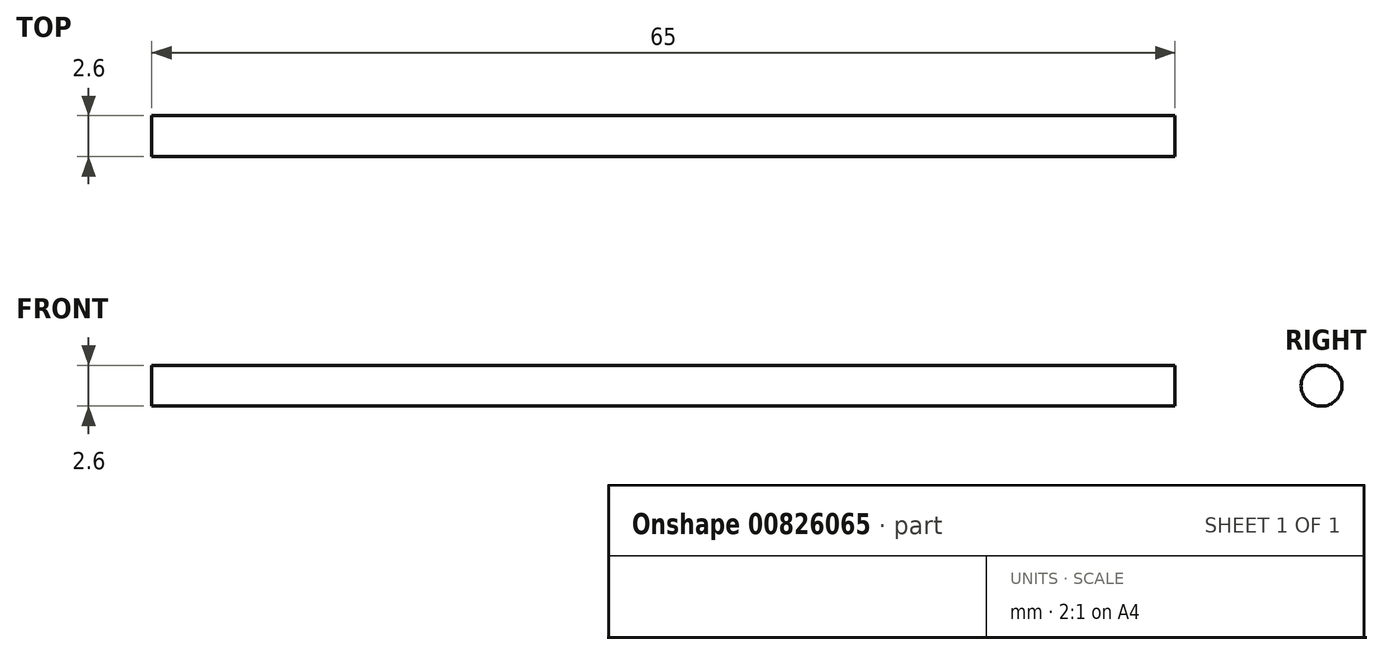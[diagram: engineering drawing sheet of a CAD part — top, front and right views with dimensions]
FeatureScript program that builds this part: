
annotation { "Feature Type Name" : "Feature", "Feature Type Description" : "" }
export const myFeature = defineFeature(function(context is Context, id is Id, definition is map)
    precondition{}
    {
        {
            var Q0;
            Q0=qCreatedBy(makeId("Right.planeOp"),FACE);
            var sketch = newSketch(context, id + "F0", { "sketchPlane" : qUnion([Q0])});
            skCircle(sketch, "E0", {"center": v(0, 0) * mm, "radius": 1.3 * mm});
            skSolve(sketch);
        }
        {
            var Q0;
            Q0=makeQuery(id+"F0.imprint","IMPRINT",FACE,{"disambiguationData":[TD([[makeQuery(id+"F0.imprint","IMPRINT",EDGE,{"derivedFrom":sQuery(id+"F0.wireOp",EDGE,"E0")}),1.0]])]});
            extrude(context, id + "F1", {"entities" : qUnion([Q0]), "depth" : 32.5 * mm, "offsetDistance" : 25 * mm});
        }
        {
            var Q0;
            Q0=makeQuery(id+"F1.opExtrude","CAP_FACE",FACE,{"disambiguationData":[OSD([sQuery(id+"F0.wireOp",EDGE,"E0")])],"isStart":true});
            extrude(context, id + "F2", {"entities" : qUnion([Q0]), "operationType" : NewBodyOperationType.ADD, "depth" : 32.5 * mm, "offsetDistance" : 25 * mm});
        }
    });
